# Revit family: FU_Chair_Sandler_Myra 5-1
name_source: partatom
category: Furniture
units: mm (PartAtom-declared; Revit-internal decimal feet)

## family parameters
Always vertical = Yes
Cut with Voids When Loaded = No
OmniClass Number = 23.40.20.00
OmniClass Title = General Furniture and Specialties
Room Calculation Point = No
Shared = No
Work Plane-Based = No

## types (1)
- Myra 5.1
    Default Elevation = 0 mm  [stored 0 ft]
    Depth = 740 mm  [stored 2.42782 ft]
    Description = Fully upholstered lounge chair on steel frame base. With contrast stitching in red or rope color.
    Frame = Metal - Paint -AL VR - Coral Red
    Height = 890 mm  [stored 2.91995 ft]
    Manufacturer = Sandler
    Model = Myra 5.1
    Seat = Fabric - Gravity - Dove CPC17
    URL = https://www.sandlerseating.com
    Width = 810 mm  [stored 2.65748 ft]

note: [stored X ft] marks values corroborated as IEEE doubles in the binary element streams (Revit-internal decimal feet)

## geometry (parser evidence)
native form markers: Sweep x5
no freeform markers — native parametric forms only
